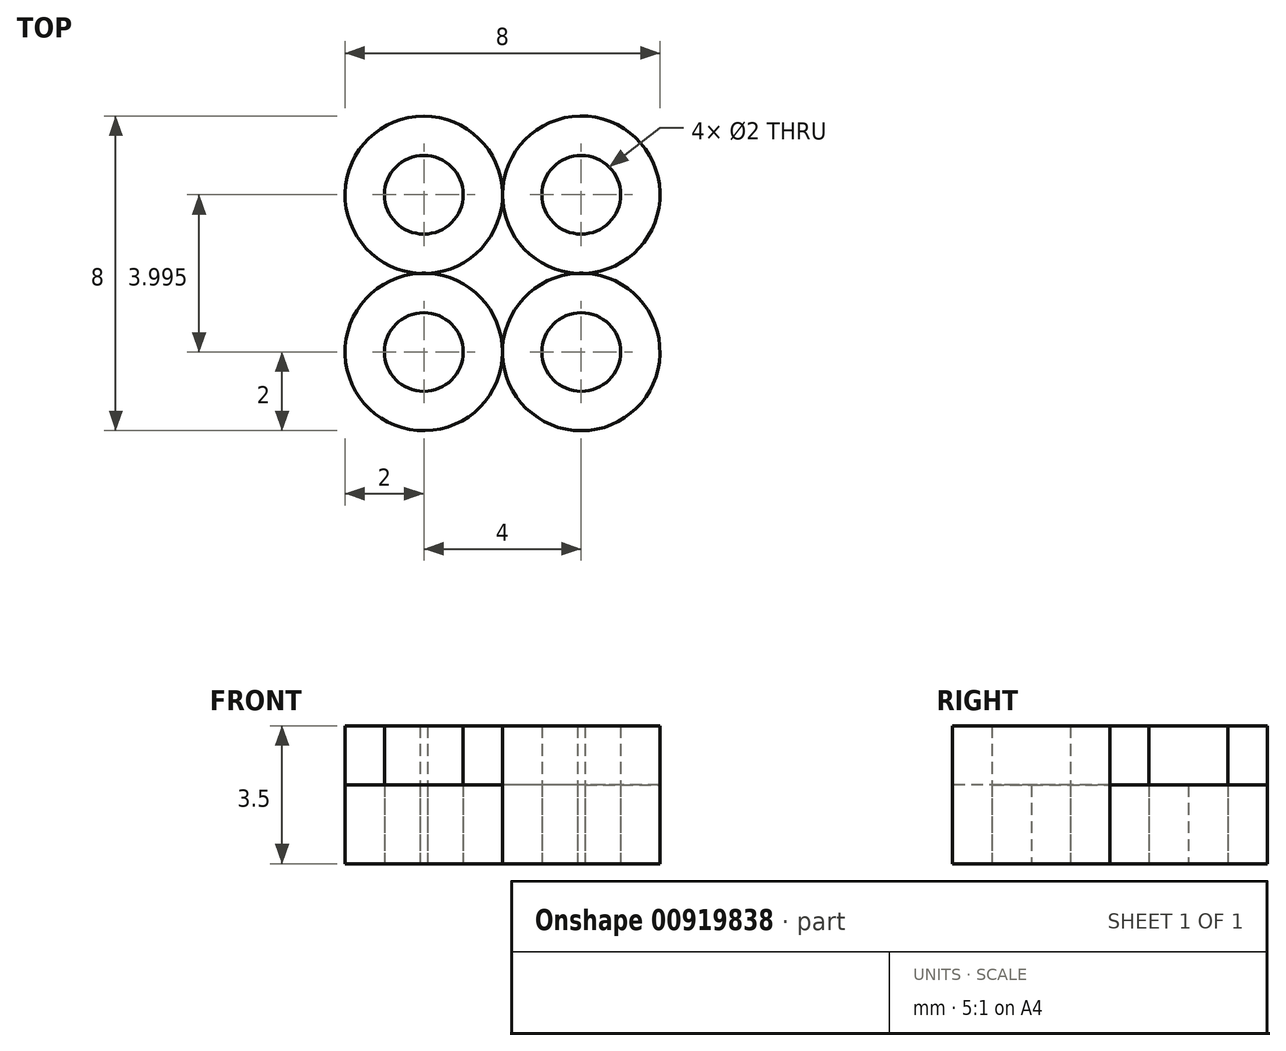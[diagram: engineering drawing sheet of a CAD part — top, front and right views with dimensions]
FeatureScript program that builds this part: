
annotation { "Feature Type Name" : "Feature", "Feature Type Description" : "" }
export const myFeature = defineFeature(function(context is Context, id is Id, definition is map)
    precondition{}
    {
        {
            var Q0;
            Q0=qCreatedBy(makeId("Top.planeOp"),FACE);
            var sketch = newSketch(context, id + "F0", { "sketchPlane" : qUnion([Q0])});
            skCircle(sketch, "E0", {"center": v(-2.4, -2.1) * mm, "radius": 1 * mm});
            skCircle(sketch, "E1.0", {"center": v(-2.4, -2.1) * mm, "radius": 2 * mm});
            skCircle(sketch, "E2.MirrorC", {"center": v(1.6, -2.1) * mm, "radius": 2 * mm});
            skCircle(sketch, "E3.MirrorC", {"center": v(1.6, -2.1) * mm, "radius": 1 * mm});
            skCircle(sketch, "E4.MirrorC", {"center": v(-2.4, 1.9) * mm, "radius": 2 * mm});
            skCircle(sketch, "E5.MirrorC", {"center": v(-2.4, 1.9) * mm, "radius": 1 * mm});
            skCircle(sketch, "E6.MirrorC", {"center": v(1.6, 1.9) * mm, "radius": 1 * mm});
            skCircle(sketch, "E7.MirrorC", {"center": v(1.6, 1.9) * mm, "radius": 2 * mm});
            skSolve(sketch);
        }
        {
            var Q0;
            Q0=makeQuery(id+"F0.imprint","IMPRINT",FACE,{"disambiguationData":[TD([[makeQuery(id+"F0.imprint","IMPRINT",EDGE,{"derivedFrom":sQuery(id+"F0.wireOp",EDGE,"E5.MirrorC")}),-1.0]])]});
            var Q1;
            Q1=makeQuery(id+"F0.imprint","IMPRINT",FACE,{"disambiguationData":[TD([[makeQuery(id+"F0.imprint","IMPRINT",EDGE,{"derivedFrom":sQuery(id+"F0.wireOp",EDGE,"E6.MirrorC")}),1.0]])]});
            var Q2;
            Q2=makeQuery(id+"F0.imprint","IMPRINT",FACE,{"disambiguationData":[TD([[makeQuery(id+"F0.imprint","IMPRINT",EDGE,{"derivedFrom":sQuery(id+"F0.wireOp",EDGE,"E3.MirrorC")}),-1.0]])]});
            var Q3;
            Q3=makeQuery(id+"F0.imprint","IMPRINT",FACE,{"disambiguationData":[TD([[makeQuery(id+"F0.imprint","IMPRINT",EDGE,{"derivedFrom":sQuery(id+"F0.wireOp",EDGE,"E0")}),1.0]])]});
            extrude(context, id + "F1", {"entities" : qUnion([Q0, Q1, Q2, Q3]), "depth" : 3.5 * mm, "offsetDistance" : 25 * mm});
        }
        {
            var Q0;
            Q0=makeQuery(id+"F0.imprint","IMPRINT",FACE,{"disambiguationData":[TD([[makeQuery(id+"F0.imprint","IMPRINT",EDGE,{"derivedFrom":sQuery(id+"F0.wireOp",EDGE,"E0")}),-1.0]])]});
            var Q1;
            Q1=makeQuery(id+"F0.imprint","IMPRINT",FACE,{"disambiguationData":[TD([[makeQuery(id+"F0.imprint","IMPRINT",EDGE,{"derivedFrom":sQuery(id+"F0.wireOp",EDGE,"E3.MirrorC")}),1.0]])]});
            var Q2;
            Q2=makeQuery(id+"F0.imprint","IMPRINT",FACE,{"disambiguationData":[TD([[makeQuery(id+"F0.imprint","IMPRINT",EDGE,{"derivedFrom":sQuery(id+"F0.wireOp",EDGE,"E6.MirrorC")}),-1.0]])]});
            var Q3;
            Q3=makeQuery(id+"F0.imprint","IMPRINT",FACE,{"disambiguationData":[TD([[makeQuery(id+"F0.imprint","IMPRINT",EDGE,{"derivedFrom":sQuery(id+"F0.wireOp",EDGE,"E5.MirrorC")}),1.0]])]});
            extrude(context, id + "F2", {"entities" : qUnion([Q0, Q1, Q2, Q3]), "depth" : 2 * mm, "offsetDistance" : 25 * mm});
        }
        {
            var Q0;
            {var subQ0=sQuery(id+"F0.wireOp",EDGE,"E2.MirrorC");var subQ1=sQuery(id+"F0.wireOp",EDGE,"E1.0");var subQ2=makeQuery(id+"F0.imprint","INTERSECT",VERTEX,{"derivedFrom":[subQ1,subQ0]});Q0=makeQuery(id+"F0.imprint","IMPRINT",FACE,{"disambiguationData":[TD([[makeQuery(id+"F0.imprint","IMPRINT",EDGE,{"disambiguationData":[TD([[subQ2,-1.0]])],"derivedFrom":subQ1}),-1.0]])]});}
            extrude(context, id + "F3", {"entities" : qUnion([Q0]), "depth" : 2 * mm, "offsetDistance" : 25 * mm});
        }
    });
